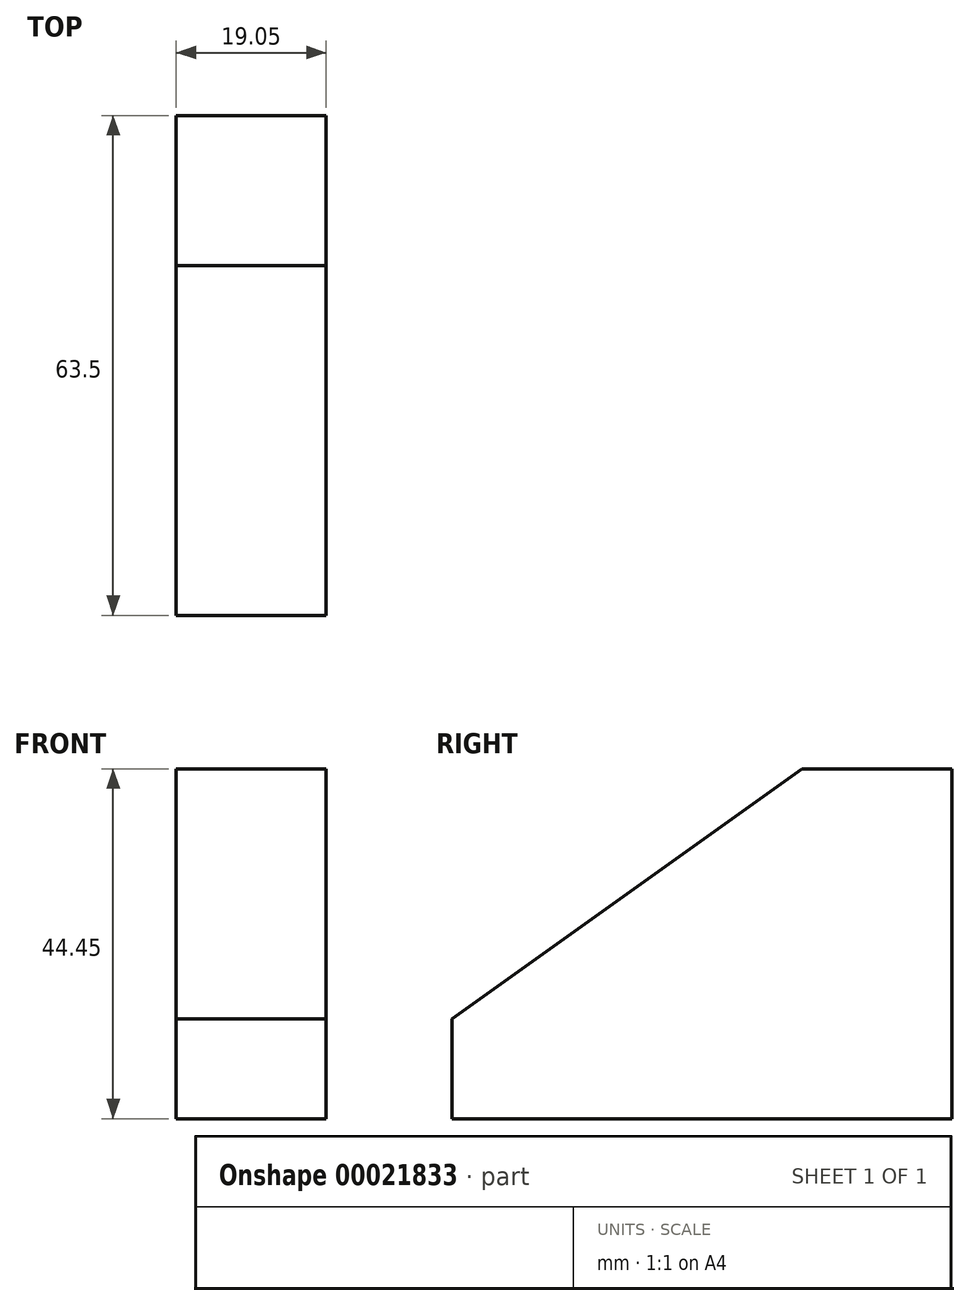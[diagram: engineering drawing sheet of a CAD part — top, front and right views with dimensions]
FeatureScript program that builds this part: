
annotation { "Feature Type Name" : "Feature", "Feature Type Description" : "" }
export const myFeature = defineFeature(function(context is Context, id is Id, definition is map)
    precondition{}
    {
        {
            var Q0;
            Q0=qCreatedBy(makeId("Right.planeOp"),FACE);
            var sketch = newSketch(context, id + "F0", { "sketchPlane" : qUnion([Q0])});
            skLineSegment(sketch, "E0", {"start": v(47.88, 16.53) * mm, "end": v(47.88, -27.92) * mm});
            skLineSegment(sketch, "E1", {"start": v(47.88, -27.92) * mm, "end": v(-15.62, -27.92) * mm});
            skLineSegment(sketch, "E2", {"start": v(-15.62, -27.92) * mm, "end": v(-15.62, -15.22) * mm});
            skLineSegment(sketch, "E3", {"start": v(47.88, 16.53) * mm, "end": v(28.83, 16.53) * mm});
            skLineSegment(sketch, "E4", {"start": v(28.83, 16.53) * mm, "end": v(-15.62, -15.22) * mm});
            skSolve(sketch);
        }
        {
            var Q0;
            Q0 = qSketchRegion(id + "F0", true);
            extrude(context, id + "F1", {"entities" : qUnion([Q0]), "depth" : 19.05 * mm});
        }
    });
